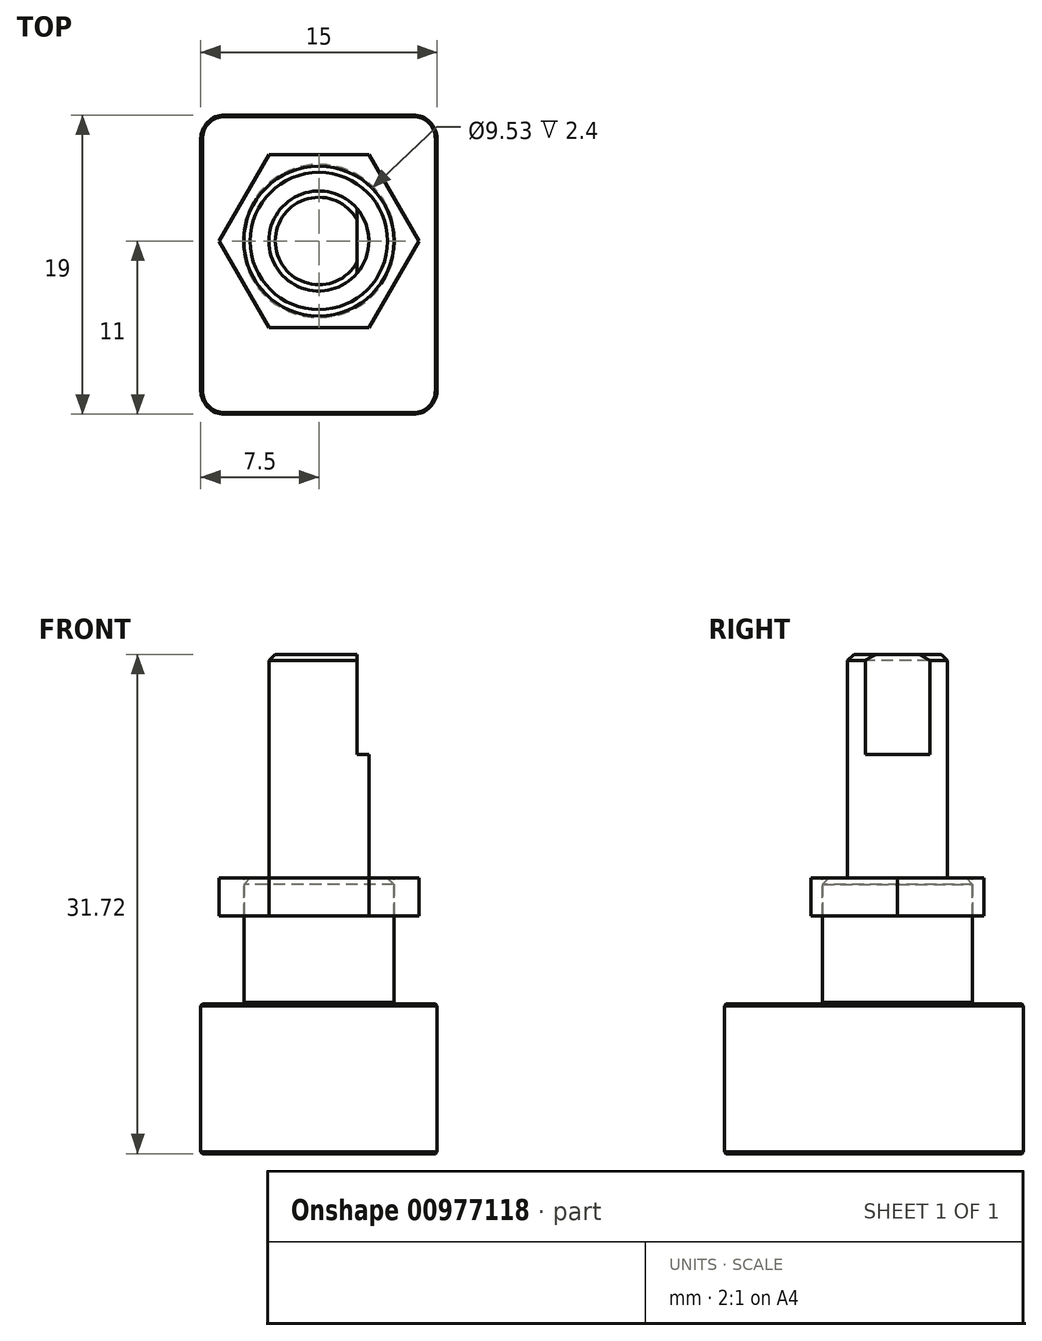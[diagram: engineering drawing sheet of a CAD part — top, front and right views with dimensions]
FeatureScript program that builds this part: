
annotation { "Feature Type Name" : "Feature", "Feature Type Description" : "" }
export const myFeature = defineFeature(function(context is Context, id is Id, definition is map)
    precondition{}
    {
        {
            var Q0;
            Q0=qCreatedBy(makeId("Top.planeOp"),FACE);
            var sketch = newSketch(context, id + "F0", { "sketchPlane" : qUnion([Q0])});
            skLineSegment(sketch, "E0.bottom", {"start": v(-7.5, 8) * mm, "end": v(7.5, 8) * mm});
            skLineSegment(sketch, "E0.left", {"start": v(-7.5, 8) * mm, "end": v(-7.5, -4.7) * mm});
            skLineSegment(sketch, "E0.right", {"start": v(7.5, 8) * mm, "end": v(7.5, -8) * mm});
            skPoint(sketch, "E1", {"position": v(0, 0) * mm});
            skPoint(sketch, "E1.positionSnap0", {"position": v(7.5, 0) * mm});
            skPoint(sketch, "E1.positionSnap1", {"position": v(0, 8) * mm});
            skLineSegment(sketch, "E2.top", {"start": v(-7.5, -11) * mm, "end": v(7.5, -11) * mm});
            skLineSegment(sketch, "E2.left", {"start": v(-7.5, -4.7) * mm, "end": v(-7.5, -11) * mm});
            skLineSegment(sketch, "E2.right", {"start": v(7.5, -8) * mm, "end": v(7.5, -11) * mm});
            skSolve(sketch);
        }
        {
            var Q0;
            Q0=qSketchRegion(id+"F0",true);
            extrude(context, id + "F1", {"entities" : qUnion([Q0]), "depth" : 9.5 * mm, "offsetDistance" : 25 * mm});
        }
        {
            var Q0;
            Q0=makeQuery(id+"F1.opExtrude","CAP_FACE",FACE,{"disambiguationData":[OSD([sQuery(id+"F0.wireOp",EDGE,"E0.bottom"),sQuery(id+"F0.wireOp",EDGE,"E0.left"),sQuery(id+"F0.wireOp",EDGE,"E0.right"),sQuery(id+"F0.wireOp",EDGE,"E2.top"),sQuery(id+"F0.wireOp",EDGE,"E2.left"),sQuery(id+"F0.wireOp",EDGE,"E2.right")])],"isStart":false});
            var sketch = newSketch(context, id + "F2", { "sketchPlane" : qUnion([Q0])});
            skCircle(sketch, "E3", {"center": v(0, 0) * mm, "radius": 4.76 * mm});
            skSolve(sketch);
        }
        {
            var Q0;
            Q0=qSketchRegion(id+"F2",true);
            extrude(context, id + "F3", {"entities" : qUnion([Q0]), "operationType" : NewBodyOperationType.ADD, "depth" : 8 * mm, "offsetDistance" : 25 * mm});
        }
        {
            var Q0;
            Q0=makeQuery(id+"F3.opExtrude","CAP_FACE",FACE,{"disambiguationData":[OSD([sQuery(id+"F2.wireOp",EDGE,"E3")])],"isStart":false});
            var sketch = newSketch(context, id + "F4", { "sketchPlane" : qUnion([Q0])});
            skCircle(sketch, "E4", {"center": v(0, 0) * mm, "radius": 3.17 * mm});
            skSolve(sketch);
        }
        {
            var Q0;
            Q0=qSketchRegion(id+"F4",true);
            extrude(context, id + "F5", {"entities" : qUnion([Q0]), "operationType" : NewBodyOperationType.ADD, "depth" : 14.22 * mm, "offsetDistance" : 25 * mm});
        }
        {
            var Q0;
            Q0=makeQuery(id+"F5.opExtrude","CAP_FACE",FACE,{"disambiguationData":[OSD([sQuery(id+"F4.wireOp",EDGE,"E4")])],"isStart":false});
            var sketch = newSketch(context, id + "F6", { "sketchPlane" : qUnion([Q0])});
            skArc(sketch, "E5.0", {"start": v(2.43, -2.05) * mm, "mid": v(3.17, 0) * mm, "end": v(2.43, 2.05) * mm});
            skLineSegment(sketch, "E6", {"start": v(2.43, 2.05) * mm, "end": v(2.43, -2.05) * mm});
            skLineSegment(sketch, "E7", {"start": v(2.43, 0) * mm, "end": v(-3.17, 0) * mm, "construction": true});
            skSolve(sketch);
        }
        {
            var Q0;
            Q0=qSketchRegion(id+"F6",true);
            extrude(context, id + "F7", {"entities" : qUnion([Q0]), "operationType" : NewBodyOperationType.REMOVE, "oppositeDirection" : true, "depth" : 6.35 * mm, "offsetDistance" : 25 * mm});
        }
        {
            var Q0;
            Q0=makeQuery(id+"F5.opExtrude","CAP_EDGE",EDGE,{"disambiguationData":[OSD([sQuery(id+"F4.wireOp",EDGE,"E4")])],"isStart":false});
            var Q1;
            Q1=makeQuery(id+"F7.boolean.opBoolean","COPY",EDGE,{"derivedFrom":makeQuery(id+"F7.opExtrude","CAP_EDGE",EDGE,{"disambiguationData":[OSD([sQuery(id+"F6.wireOp",EDGE,"E6")])],"isStart":true})});
            var Q2;
            Q2=makeQuery(id+"F3.opExtrude","CAP_EDGE",EDGE,{"disambiguationData":[OSD([sQuery(id+"F2.wireOp",EDGE,"E3")])],"isStart":false});
            chamfer(context, id + "F8", {"entities" : qUnion([Q0, Q1, Q2]), "width" : .4 * mm, "tangentPropagation" : true});
        }
        {
            var Q0;
            Q0=makeQuery(id+"F1.opExtrude","SWEPT_EDGE",EDGE,{"disambiguationData":[OSD([sQuery(id+"F0.wireOp",EDGE,"E2.top"),sQuery(id+"F0.wireOp",EDGE,"E2.left")])]});
            var Q1;
            Q1=makeQuery(id+"F1.opExtrude","SWEPT_EDGE",EDGE,{"disambiguationData":[OSD([sQuery(id+"F0.wireOp",EDGE,"E2.top"),sQuery(id+"F0.wireOp",EDGE,"E2.right")])]});
            var Q2;
            Q2=makeQuery(id+"F1.opExtrude","SWEPT_EDGE",EDGE,{"disambiguationData":[OSD([sQuery(id+"F0.wireOp",EDGE,"E0.bottom"),sQuery(id+"F0.wireOp",EDGE,"E0.right")])]});
            var Q3;
            Q3=makeQuery(id+"F1.opExtrude","SWEPT_EDGE",EDGE,{"disambiguationData":[OSD([sQuery(id+"F0.wireOp",EDGE,"E0.bottom"),sQuery(id+"F0.wireOp",EDGE,"E0.left")])]});
            fillet(context, id + "F9", {"entities" : qUnion([Q0, Q1, Q2, Q3]), "radius" : 1.5 * mm, "tangentPropagation" : true, "allowEdgeOverflow" : false});
        }
        {
            var Q0;
            Q0=makeQuery(id+"F1.opExtrude","CAP_FACE",FACE,{"disambiguationData":[OSD([sQuery(id+"F0.wireOp",EDGE,"E0.bottom"),sQuery(id+"F0.wireOp",EDGE,"E0.left"),sQuery(id+"F0.wireOp",EDGE,"E0.right"),sQuery(id+"F0.wireOp",EDGE,"E2.top"),sQuery(id+"F0.wireOp",EDGE,"E2.left"),sQuery(id+"F0.wireOp",EDGE,"E2.right")])],"isStart":false});
            var Q1;
            Q1=makeQuery(id+"F1.opExtrude","CAP_FACE",FACE,{"disambiguationData":[OSD([sQuery(id+"F0.wireOp",EDGE,"E0.bottom"),sQuery(id+"F0.wireOp",EDGE,"E0.left"),sQuery(id+"F0.wireOp",EDGE,"E0.right"),sQuery(id+"F0.wireOp",EDGE,"E2.top"),sQuery(id+"F0.wireOp",EDGE,"E2.left"),sQuery(id+"F0.wireOp",EDGE,"E2.right")])],"isStart":true});
            chamfer(context, id + "F10", {"entities" : qUnion([Q0, Q1]), "width" : .1 * mm, "tangentPropagation" : true});
        }
        {
            var Q0;
            Q0=makeQuery(id+"F3.opExtrude","CAP_FACE",FACE,{"disambiguationData":[OSD([sQuery(id+"F2.wireOp",EDGE,"E3")])],"isStart":false});
            var sketch = newSketch(context, id + "F11", { "sketchPlane" : qUnion([Q0])});
            skCircle(sketch, "E8.0", {"center": v(0, 0) * mm, "radius": 4.76 * mm});
            skCircle(sketch, "E9.cCircle", {"center": v(0, 0) * mm, "radius": 5.5 * mm, "construction": true});
            skLineSegment(sketch, "E9.0", {"start": v(-3.18, 5.5) * mm, "end": v(3.18, 5.5) * mm});
            skLineSegment(sketch, "E9.1", {"start": v(3.18, 5.5) * mm, "end": v(6.35, 0) * mm});
            skLineSegment(sketch, "E9.2", {"start": v(6.35, 0) * mm, "end": v(3.18, -5.5) * mm});
            skLineSegment(sketch, "E9.3", {"start": v(3.18, -5.5) * mm, "end": v(-3.18, -5.5) * mm});
            skLineSegment(sketch, "E9.4", {"start": v(-3.18, -5.5) * mm, "end": v(-6.35, 0) * mm});
            skLineSegment(sketch, "E9.5", {"start": v(-6.35, 0) * mm, "end": v(-3.18, 5.5) * mm});
            skPoint(sketch, "E9.0.midPoint", {"position": v(0, 5.5) * mm});
            skSolve(sketch);
        }
        {
            var Q0;
            Q0 = qSketchRegion(id + "F11", true);
            extrude(context, id + "F12", {"entities" : qUnion([Q0]), "oppositeDirection" : true, "depth" : 2.4 * mm, "offsetDistance" : 25 * mm});
        }
    });
